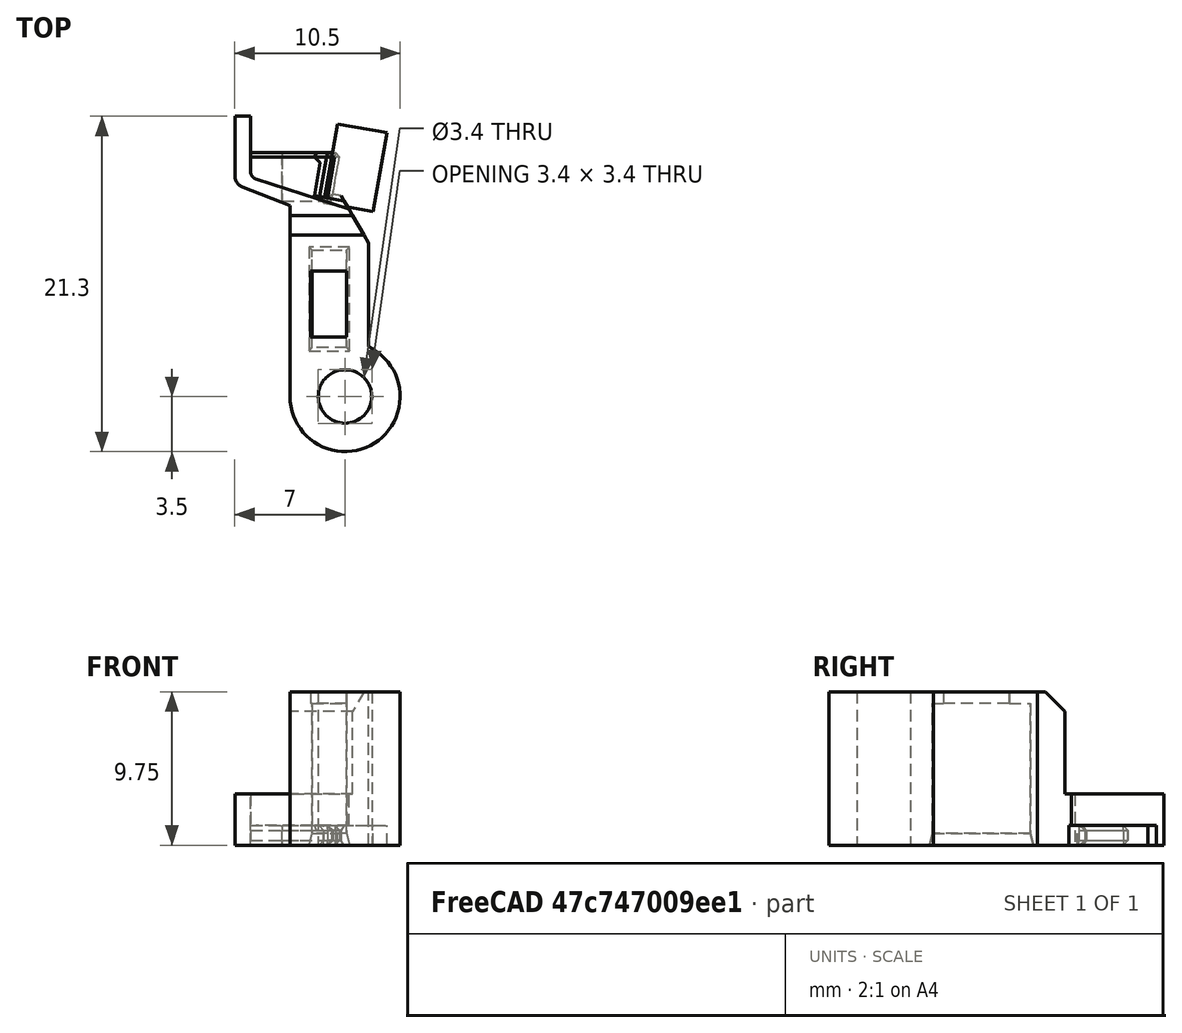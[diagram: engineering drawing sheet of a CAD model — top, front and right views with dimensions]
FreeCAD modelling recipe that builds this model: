
FCSTD DOCUMENT  (FreeCAD 0.18R14555 (Git shallow))
Label: filament-sensor-arm
License: All rights reserved
LicenseURL: http://en.wikipedia.org/wiki/All_rights_reserved
objects: Part::Feature×5, Part::Box×4, Part::Cut×2, Part::Chamfer×2, Part::MultiFuse×2
note: 15 computed .brp shape members not serialized (recipe doc carries the construction recipe); baked Part::Feature solids carry a one-line shape summary decoded from their .brp

FEATURE [Part::Feature] Part__Feature004001  label="fs-lever_002"
  Placement = pos=(9.88832e-05,-0.000145151,1.25173) rot=(2.9e-05,1,0;3.14159rad)
  shape: bbox 10.5 x 21.3 x 9.75 mm, 45 faces (baked)
FEATURE [Part::Box] Box  label="0.5"
  AttacherType = Attacher::AttachEngine3D
  Height = 1.25
  Length = 3.2
  Placement = pos=(-4,12.4,0) rot=(0,0,1;0rad)
  Width = 3.1
FEATURE [Part::Box] Box001  label="0.006"
  AttacherType = Attacher::AttachEngine3D
  Height = 1.25
  Length = 3.7
  Placement = pos=(-4,12.4,0) rot=(0,0,1;0rad)
  Width = 3.1
FEATURE [Part::Feature] Part__Feature004002  label="fs-lever_003"
  Placement = pos=(9.88832e-05,-0.000145151,1.25173) rot=(2.9e-05,1,0;3.14159rad)
  shape: bbox 10.5 x 21.3 x 9.75 mm, 45 faces (baked)
FEATURE [Part::Box] Box003  label="cut001"
  AttacherType = Attacher::AttachEngine3D
  Height = 1.25
  Length = 3.2
  Placement = pos=(-1.3715,12.2971,0) rot=(0,0,-1;0.174533rad)
  Width = 5.1
FEATURE [Part::Box] Box004  label="cut002"
  AttacherType = Attacher::AttachEngine3D
  Height = 1.25
  Length = 3.2
  Placement = pos=(-1.3715,12.2971,0) rot=(0,0,-1;0.174533rad)
  Width = 5.1
FEATURE [Part::Cut] Cut
  Base = -> Box
  Tool = -> Box004
FEATURE [Part::Chamfer] Chamfer  label="05mm-ext"
  Base = -> Cut
  Edges = 5 edges r=0.3: [Edge8,Edge9,Edge10,Edge11,Edge12]
FEATURE [Part::Feature] Box003001  label="cut003"
  Placement = pos=(0.5,0,0) rot=(0,0,1;0rad)
  shape: bbox 4.037 x 5.578 x 1.25 mm, 6 faces (baked)
FEATURE [Part::Cut] Cut001
  Base = -> Box001
  Tool = -> Box003001
FEATURE [Part::Chamfer] Chamfer001  label="10mm-ext"
  Base = -> Cut001
  Edges = 5 edges r=0.3: [Edge8,Edge9,Edge10,Edge11,Edge12]
FEATURE [Part::Feature] Chamfer001001  label="10mm-ext001"
  shape: bbox 3.641 x 3.1 x 1.25 mm, 13 faces (baked)
FEATURE [Part::Feature] Chamfer001002  label="05mm-ext001"
  shape: bbox 3.141 x 3.1 x 1.25 mm, 13 faces (baked)
FEATURE [Part::MultiFuse] Fusion
  Shapes = -> [Part__Feature004002,Chamfer001001]
FEATURE [Part::MultiFuse] Fusion001  label="extend-5mm"
  Shapes = -> [Chamfer001002,Part__Feature004001]
